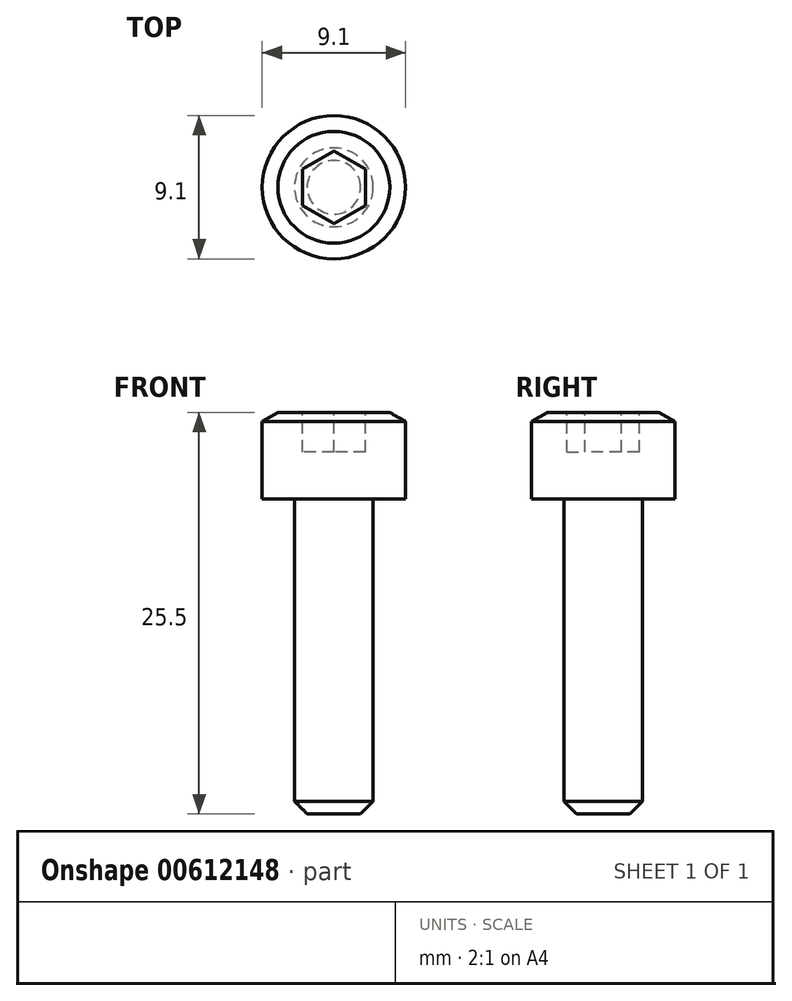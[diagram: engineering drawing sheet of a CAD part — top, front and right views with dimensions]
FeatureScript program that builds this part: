
annotation { "Feature Type Name" : "Feature", "Feature Type Description" : "" }
export const myFeature = defineFeature(function(context is Context, id is Id, definition is map)
    precondition{}
    {
        {
            var Q0;
            Q0=qCreatedBy(makeId("Top.planeOp"),FACE);
            var sketch = newSketch(context, id + "F0", { "sketchPlane" : qUnion([Q0])});
            skCircle(sketch, "E0", {"center": v(0, 0) * mm, "radius": 4.55 * mm});
            skSolve(sketch);
        }
        {
            var Q0;
            Q0=makeQuery(id+"F0.imprint","IMPRINT",FACE,{"disambiguationData":[TD([[makeQuery(id+"F0.imprint","IMPRINT",EDGE,{"derivedFrom":sQuery(id+"F0.wireOp",EDGE,"E0")}),1.0]])]});
            extrude(context, id + "F1", {"entities" : qUnion([Q0]), "oppositeDirection" : true, "depth" : 5.5 * mm, "offsetDistance" : 25 * mm});
        }
        {
            var Q0;
            Q0=makeQuery(id+"F1.opExtrude","CAP_FACE",FACE,{"disambiguationData":[OSD([sQuery(id+"F0.wireOp",EDGE,"E0")])],"isStart":false});
            var sketch = newSketch(context, id + "F2", { "sketchPlane" : qUnion([Q0])});
            skCircle(sketch, "E1", {"center": v(0, 0) * mm, "radius": 2.5 * mm});
            skSolve(sketch);
        }
        {
            var Q0;
            Q0=makeQuery(id+"F2.imprint","IMPRINT",FACE,{"disambiguationData":[TD([[makeQuery(id+"F2.imprint","IMPRINT",EDGE,{"derivedFrom":sQuery(id+"F2.wireOp",EDGE,"E1")}),1.0]])]});
            extrude(context, id + "F3", {"entities" : qUnion([Q0]), "operationType" : NewBodyOperationType.ADD, "depth" : 20 * mm, "offsetDistance" : 25 * mm});
        }
        {
            var Q0;
            Q0=makeQuery(id+"F1.opExtrude","CAP_FACE",FACE,{"disambiguationData":[OSD([sQuery(id+"F0.wireOp",EDGE,"E0")])],"isStart":true});
            var sketch = newSketch(context, id + "F4", { "sketchPlane" : qUnion([Q0])});
            skCircle(sketch, "E2.cCircle", {"center": v(0, 0) * mm, "radius": 2.3 * mm, "construction": true});
            skLineSegment(sketch, "E2.0", {"start": v(0, -2.3) * mm, "end": v(-2, -1.15) * mm});
            skLineSegment(sketch, "E2.1", {"start": v(-2, -1.15) * mm, "end": v(-2, 1.15) * mm});
            skLineSegment(sketch, "E2.2", {"start": v(-2, 1.15) * mm, "end": v(0, 2.3) * mm});
            skLineSegment(sketch, "E2.3", {"start": v(0, 2.3) * mm, "end": v(2, 1.15) * mm});
            skLineSegment(sketch, "E2.4", {"start": v(2, 1.15) * mm, "end": v(2, -1.15) * mm});
            skLineSegment(sketch, "E2.5", {"start": v(2, -1.15) * mm, "end": v(0, -2.3) * mm});
            skSolve(sketch);
        }
        {
            var Q0;
            Q0=makeQuery(id+"F4.imprint","IMPRINT",FACE,{"disambiguationData":[TD([[makeQuery(id+"F4.imprint","IMPRINT",EDGE,{"derivedFrom":sQuery(id+"F4.wireOp",EDGE,"E2.0")}),-1.0]])]});
            extrude(context, id + "F5", {"entities" : qUnion([Q0]), "operationType" : NewBodyOperationType.REMOVE, "oppositeDirection" : true, "depth" : 2.5 * mm, "offsetDistance" : 25 * mm});
        }
        {
            var Q0;
            Q0=makeQuery(id+"F1.opExtrude","CAP_EDGE",EDGE,{"disambiguationData":[OSD([sQuery(id+"F0.wireOp",EDGE,"E0")])],"isStart":true});
            chamfer(context, id + "F6", {"entities" : qUnion([Q0]), "chamferType" : ChamferType.OFFSET_ANGLE, "width" : 1 * mm, "oppositeDirection" : false, "angle" : 30 * degree, "tangentPropagation" : true});
        }
        {
            var Q0;
            Q0=makeQuery(id+"F3.opExtrude","CAP_EDGE",EDGE,{"disambiguationData":[OSD([sQuery(id+"F2.wireOp",EDGE,"E1")])],"isStart":false});
            chamfer(context, id + "F7", {"entities" : qUnion([Q0]), "width" : 0.8 * mm, "tangentPropagation" : true});
        }
    });
